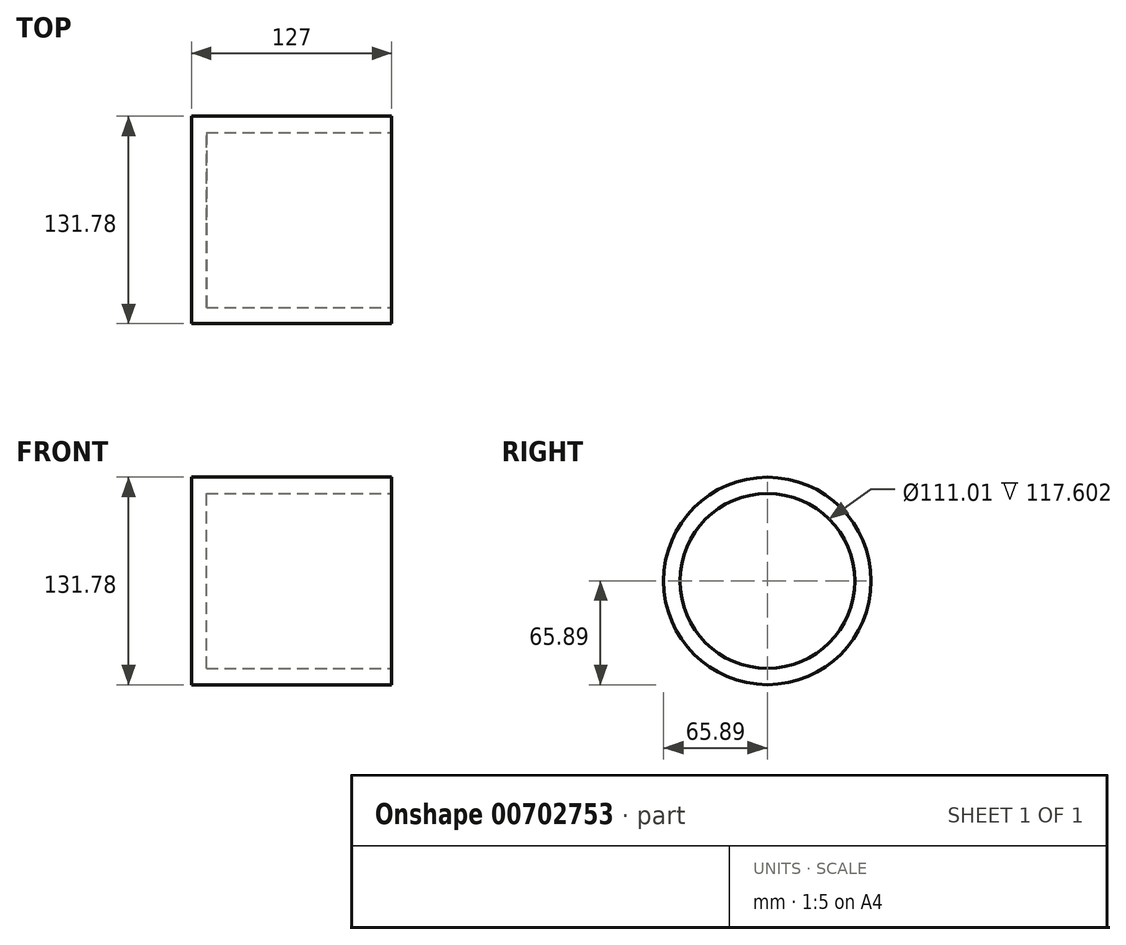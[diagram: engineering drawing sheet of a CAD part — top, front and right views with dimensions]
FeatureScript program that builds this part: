
annotation { "Feature Type Name" : "Feature", "Feature Type Description" : "" }
export const myFeature = defineFeature(function(context is Context, id is Id, definition is map)
    precondition{}
    {
        {
            var Q0;
            Q0=qCreatedBy(makeId("Right.planeOp"),FACE);
            var sketch = newSketch(context, id + "F0", { "sketchPlane" : qUnion([Q0])});
            skCircle(sketch, "E0", {"center": v(0, 0) * mm, "radius": 65.89 * mm});
            skSolve(sketch);
        }
        {
            var Q0;
            Q0=makeQuery(id+"F0.imprint","IMPRINT",FACE,{"disambiguationData":[TD([[makeQuery(id+"F0.imprint","IMPRINT",EDGE,{"derivedFrom":sQuery(id+"F0.wireOp",EDGE,"E0")}),1.0]])]});
            extrude(context, id + "F1", {"entities" : qUnion([Q0]), "depth" : 127 * mm, "offsetDistance" : 25.4 * mm});
        }
        {
            var Q0;
            Q0=makeQuery(id+"F1.opExtrude","CAP_FACE",FACE,{"disambiguationData":[OSD([sQuery(id+"F0.wireOp",EDGE,"E0")])],"isStart":false});
            var sketch = newSketch(context, id + "F2", { "sketchPlane" : qUnion([Q0])});
            skCircle(sketch, "E1", {"center": v(0, 0) * mm, "radius": 55.5 * mm});
            skSolve(sketch);
        }
        {
            var Q0;
            Q0 = qSketchRegion(id + "F2", true);
            extrude(context, id + "F3", {"entities" : qUnion([Q0]), "operationType" : NewBodyOperationType.REMOVE, "oppositeDirection" : true, "depth" : 117.6 * mm, "offsetDistance" : 25.4 * mm});
        }
    });
